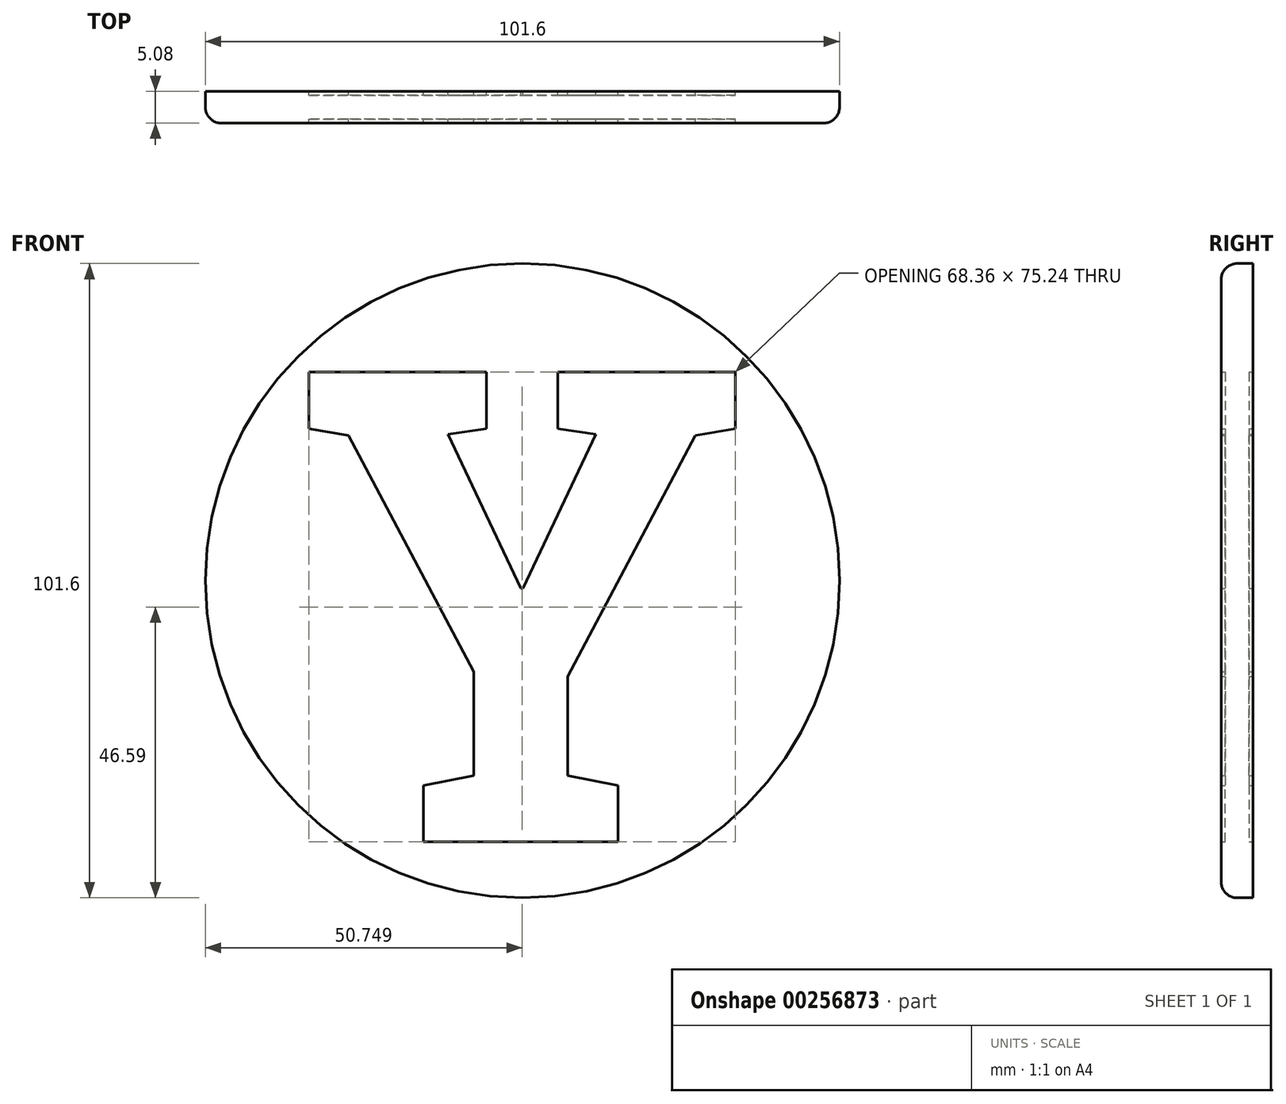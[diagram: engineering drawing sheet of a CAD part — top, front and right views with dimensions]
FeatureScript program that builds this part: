
annotation { "Feature Type Name" : "Feature", "Feature Type Description" : "" }
export const myFeature = defineFeature(function(context is Context, id is Id, definition is map)
    precondition{}
    {
        {
            var Q0;
            Q0=qCreatedBy(makeId("Front.planeOp"),FACE);
            var sketch = newSketch(context, id + "F0", { "sketchPlane" : qUnion([Q0])});
            skCircle(sketch, "E0", {"center": v(0, 0) * mm, "radius": 50.8 * mm});
            skText(sketch, "E1", { "text": "Y", "fontName": "RobotoSlab-Bold.ttf"});
            const initialGuessF0  = {"E1": [-0.0361, -0.04183, 1, 0, 0.0762]};
            skSetInitialGuess(sketch, initialGuessF0);
            skSolve(sketch);
        }
        {
            var Q0;
            Q0=makeQuery(id+"F0.imprint","IMPRINT",FACE,{"disambiguationData":[TD([[makeQuery(id+"F0.imprint","IMPRINT",EDGE,{"derivedFrom":sQuery(id+"F0.wireOp",EDGE,"E1.sketch_text.stroke-0")}),-1.0]])]});
            extrude(context, id + "F1", {"entities" : qUnion([Q0]), "endBound" : BoundingType.SYMMETRIC, "depth" : 3.8 * mm});
        }
        {
            var Q0;
            Q0=qSketchRegion(id+"F0",true);
            extrude(context, id + "F2", {"entities" : qUnion([Q0]), "operationType" : NewBodyOperationType.ADD, "endBound" : BoundingType.SYMMETRIC, "depth" : 5.08 * mm});
        }
        {
            var Q0;
            Q0=makeQuery(id+"F2.opExtrude","CAP_EDGE",EDGE,{"disambiguationData":[OSD([sQuery(id+"F0.wireOp",EDGE,"E0")])],"isStart":false});
            fillet(context, id + "F3", {"entities" : qUnion([Q0]), "radius" : 2.54 * mm, "tangentPropagation" : true, "allowEdgeOverflow" : false});
        }
    });
